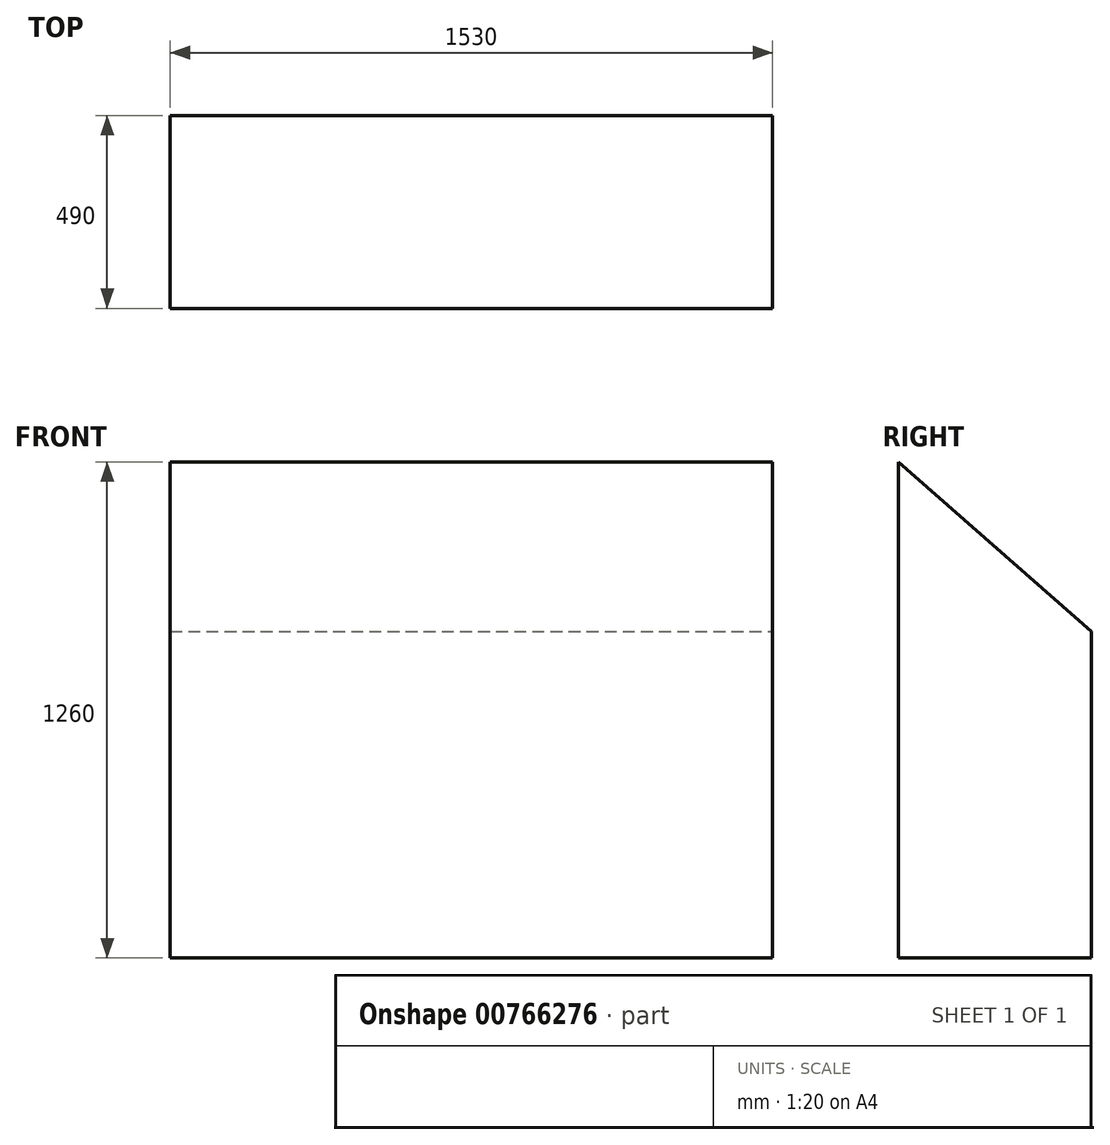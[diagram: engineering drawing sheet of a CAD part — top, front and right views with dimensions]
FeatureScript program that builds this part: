
annotation { "Feature Type Name" : "Feature", "Feature Type Description" : "" }
export const myFeature = defineFeature(function(context is Context, id is Id, definition is map)
    precondition{}
    {
        {
            var Q0;
            Q0=qCreatedBy(makeId("Right.planeOp"),FACE);
            var sketch = newSketch(context, id + "F0", { "sketchPlane" : qUnion([Q0])});
            skLineSegment(sketch, "E0", {"start": v(0, 0) * mm, "end": v(-490, 0) * mm});
            skLineSegment(sketch, "E1", {"start": v(-490, 0) * mm, "end": v(-490, 1260) * mm});
            skLineSegment(sketch, "E2", {"start": v(-490, 1260) * mm, "end": v(0, 830) * mm});
            skLineSegment(sketch, "E3", {"start": v(0, 830) * mm, "end": v(0, 0) * mm});
            skSolve(sketch);
        }
        {
            var Q0;
            Q0=makeQuery(id+"F0.imprint","IMPRINT",FACE,{"disambiguationData":[TD([[makeQuery(id+"F0.imprint","IMPRINT",EDGE,{"derivedFrom":sQuery(id+"F0.wireOp",EDGE,"E0")}),-1.0]])]});
            extrude(context, id + "F1", {"entities" : qUnion([Q0]), "oppositeDirection" : true, "depth" : 1530 * mm, "offsetDistance" : 25 * mm});
        }
    });
